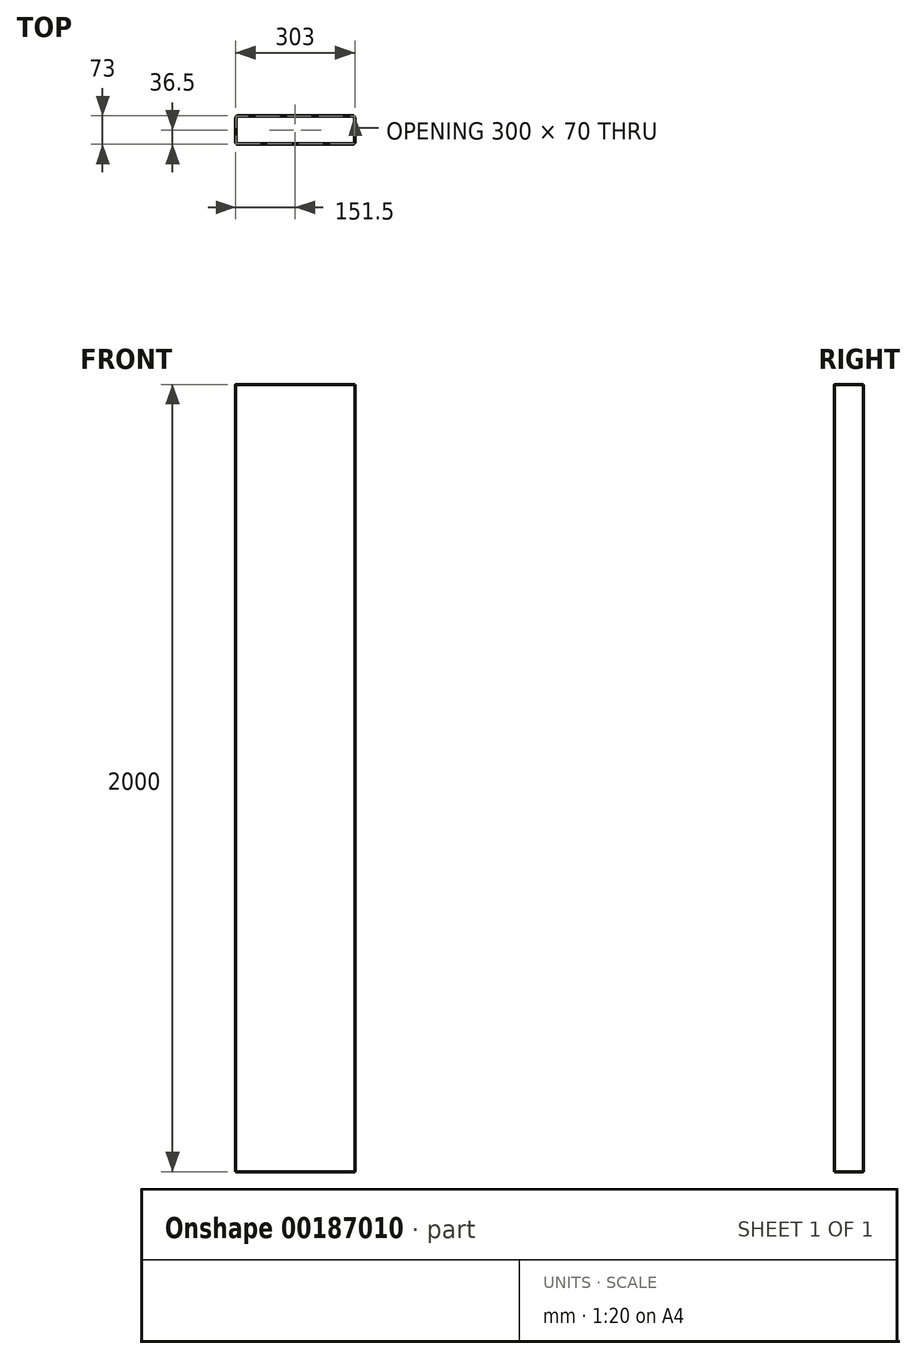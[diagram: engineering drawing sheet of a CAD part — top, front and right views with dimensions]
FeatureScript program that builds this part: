
annotation { "Feature Type Name" : "Feature", "Feature Type Description" : "" }
export const myFeature = defineFeature(function(context is Context, id is Id, definition is map)
    precondition{}
    {
        {
            var Q0;
            Q0=qCreatedBy(makeId("Top.planeOp"),FACE);
            var sketch = newSketch(context, id + "F0", { "sketchPlane" : qUnion([Q0])});
            skLineSegment(sketch, "E0.bottom", {"start": v(145, -35) * mm, "end": v(-145, -35) * mm});
            skLineSegment(sketch, "E0.top", {"start": v(145, 35) * mm, "end": v(-145, 35) * mm});
            skLineSegment(sketch, "E0.left", {"start": v(150, -30) * mm, "end": v(150, 30) * mm});
            skLineSegment(sketch, "E0.right", {"start": v(-150, -30) * mm, "end": v(-150, 30) * mm});
            skPoint(sketch, "E0.middle", {"position": v(0, 0) * mm});
            skPoint(sketch, "E1.visualSharp", {"position": v(-150, 35) * mm});
            skArc(sketch, "E1.filletArc", {"start": v(-145, 35) * mm, "mid": v(-148.54, 33.54) * mm, "end": v(-150, 30) * mm});
            skPoint(sketch, "E2.visualSharp", {"position": v(-150, -35) * mm});
            skArc(sketch, "E2.filletArc", {"start": v(-150, -30) * mm, "mid": v(-148.54, -33.54) * mm, "end": v(-145, -35) * mm});
            skPoint(sketch, "E3.visualSharp", {"position": v(150, -35) * mm});
            skArc(sketch, "E3.filletArc", {"start": v(145, -35) * mm, "mid": v(148.54, -33.54) * mm, "end": v(150, -30) * mm});
            skPoint(sketch, "E4.visualSharp", {"position": v(150, 35) * mm});
            skArc(sketch, "E4.filletArc", {"start": v(150, 30) * mm, "mid": v(148.54, 33.54) * mm, "end": v(145, 35) * mm});
            skArc(sketch, "E5.0", {"start": v(151.5, 30) * mm, "mid": v(149.6, 34.6) * mm, "end": v(145, 36.5) * mm});
            skLineSegment(sketch, "E5.1", {"start": v(151.5, -30) * mm, "end": v(151.5, 30) * mm});
            skLineSegment(sketch, "E5.2", {"start": v(145, 36.5) * mm, "end": v(-145, 36.5) * mm});
            skArc(sketch, "E5.3", {"start": v(145, -36.5) * mm, "mid": v(149.6, -34.6) * mm, "end": v(151.5, -30) * mm});
            skArc(sketch, "E5.4", {"start": v(-145, 36.5) * mm, "mid": v(-149.6, 34.6) * mm, "end": v(-151.5, 30) * mm});
            skLineSegment(sketch, "E5.5", {"start": v(-151.5, -30) * mm, "end": v(-151.5, 30) * mm});
            skArc(sketch, "E5.6", {"start": v(-151.5, -30) * mm, "mid": v(-149.6, -34.6) * mm, "end": v(-145, -36.5) * mm});
            skLineSegment(sketch, "E5.7", {"start": v(145, -36.5) * mm, "end": v(-145, -36.5) * mm});
            skSolve(sketch);
        }
        {
            var Q0;
            Q0=makeQuery(id+"F0.imprint","IMPRINT",FACE,{"disambiguationData":[TD([[makeQuery(id+"F0.imprint","IMPRINT",EDGE,{"derivedFrom":sQuery(id+"F0.wireOp",EDGE,"E0.bottom")}),1.0]])]});
            extrude(context, id + "F1", {"entities" : qUnion([Q0]), "depth" : 1000 * mm, "hasSecondDirection" : true, "secondDirectionOppositeDirection" : true, "secondDirectionDepth" : 1000 * mm});
        }
    });
